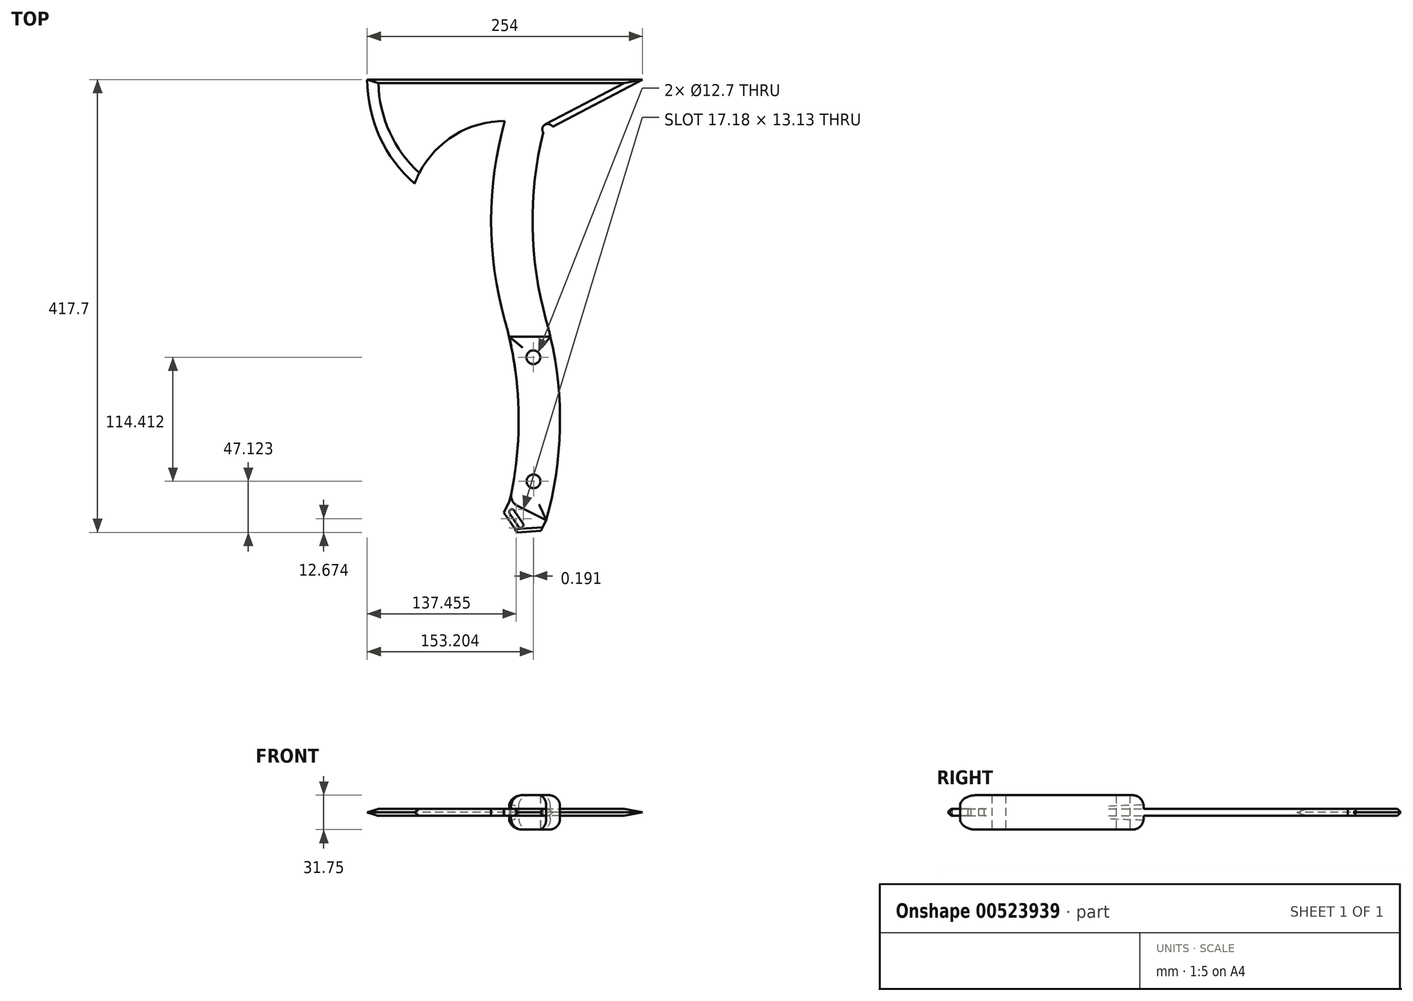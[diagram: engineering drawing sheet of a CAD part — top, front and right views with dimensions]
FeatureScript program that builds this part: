
annotation { "Feature Type Name" : "Feature", "Feature Type Description" : "" }
export const myFeature = defineFeature(function(context is Context, id is Id, definition is map)
    precondition{}
    {
        {
            var Q0;
            Q0=qCreatedBy(makeId("Top.planeOp"),FACE);
            var sketch = newSketch(context, id + "F0", { "sketchPlane" : qUnion([Q0])});
            skLineSegment(sketch, "E0.top", {"start": v(0, 496.54) * mm, "end": v(-254, 496.54) * mm});
            skLineSegment(sketch, "E1.top", {"start": v(-254, 496.54) * mm, "end": v(-139.7, 496.54) * mm});
            skLineSegment(sketch, "E2.bottom", {"start": v(-127, 496.54) * mm, "end": v(-88.9, 496.54) * mm});
            skLineSegment(sketch, "E3.bottom", {"start": v(-127, 496.54) * mm, "end": v(-139.7, 496.54) * mm});
            skArc(sketch, "E4.trimOffspring", {"start": v(-254, 496.54) * mm, "mid": v(-242.55, 443.85) * mm, "end": v(-210.28, 400.66) * mm});
            skArc(sketch, "E5", {"start": v(-127, 458.44) * mm, "mid": v(-177.68, 442.58) * mm, "end": v(-210.28, 400.66) * mm});
            skArc(sketch, "E6", {"start": v(-127, 458.44) * mm, "mid": v(-139.7, 366.37) * mm, "end": v(-127, 274.3) * mm});
            skArc(sketch, "E7", {"start": v(-91.54, 448.48) * mm, "mid": v(-101.56, 361.21) * mm, "end": v(-88.9, 274.3) * mm});
            skArc(sketch, "E8", {"start": v(-88.9, 90.14) * mm, "mid": v(-76.2, 182.22) * mm, "end": v(-88.9, 274.3) * mm});
            skArc(sketch, "E9", {"start": v(-121.56, 112.3) * mm, "mid": v(-114.5, 193.63) * mm, "end": v(-127, 274.3) * mm});
            skLineSegment(sketch, "E10", {"start": v(0, 496.54) * mm, "end": v(-91.54, 448.48) * mm});
            skPoint(sketch, "E11.end.orphan", {"position": v(-88.9, 449.87) * mm});
            skPoint(sketch, "E12.orphan", {"position": v(-88.9, 458.44) * mm});
            skLineSegment(sketch, "E13.0", {"start": v(-88.9, 90.14) * mm, "end": v(-93.76, 80.28) * mm});
            skLineSegment(sketch, "E13.1", {"start": v(-93.76, 80.28) * mm, "end": v(-115.71, 78.84) * mm});
            skLineSegment(sketch, "E13.2", {"start": v(-115.71, 78.84) * mm, "end": v(-127.94, 97.13) * mm});
            skLineSegment(sketch, "E13.3", {"start": v(-127.94, 97.13) * mm, "end": v(-123.07, 107) * mm});
            skPoint(sketch, "E13.0.midPoint", {"position": v(-88.9, 90.14) * mm});
            skLineSegment(sketch, "E14", {"start": v(-123.07, 107) * mm, "end": v(-121.56, 112.3) * mm});
            skLineSegment(sketch, "E15", {"start": v(-88.9, 90.14) * mm, "end": v(-123.07, 107) * mm});
            skPoint(sketch, "E16.orphan", {"position": v(-94.6, 92.95) * mm});
            skLineSegment(sketch, "E17.MirrorCS", {"start": v(-118.5, 99.02) * mm, "end": v(-110.36, 86.83) * mm});
            skLineSegment(sketch, "E18.MirrorCS", {"start": v(-122.73, 96.2) * mm, "end": v(-114.58, 84) * mm});
            skArc(sketch, "E19.MirrorCS", {"start": v(-110.36, 86.83) * mm, "mid": v(-111.06, 83.3) * mm, "end": v(-114.58, 84) * mm});
            skArc(sketch, "E20.MirrorCS", {"start": v(-122.73, 96.2) * mm, "mid": v(-122.03, 99.72) * mm, "end": v(-118.5, 99.02) * mm});
            skSolve(sketch);
        }
        {
            var Q0;
            Q0=makeQuery(id+"F0.imprint","IMPRINT",FACE,{"disambiguationData":[TD([[makeQuery(id+"F0.imprint","IMPRINT",EDGE,{"derivedFrom":sQuery(id+"F0.wireOp",EDGE,"E0.top")}),1.0]])]});
            var Q1;
            Q1=makeQuery(id+"F0.imprint","IMPRINT",FACE,{"disambiguationData":[TD([[makeQuery(id+"F0.imprint","IMPRINT",EDGE,{"derivedFrom":sQuery(id+"F0.wireOp",EDGE,"E13.0")}),-1.0]])]});
            extrude(context, id + "F1", {"entities" : qUnion([Q0, Q1]), "depth" : 6.35 * mm, "offsetDistance" : 25.4 * mm});
        }
        {
            var Q0;
            Q0=makeQuery(id+"F1.opExtrude","CAP_EDGE",EDGE,{"disambiguationData":[OSD([sQuery(id+"F0.wireOp",EDGE,"E4.trimOffspring")])],"isStart":false});
            var Q1;
            Q1=makeQuery(id+"F1.opExtrude","CAP_EDGE",EDGE,{"disambiguationData":[OSD([sQuery(id+"F0.wireOp",EDGE,"E4.trimOffspring")])],"isStart":true});
            chamfer(context, id + "F2", {"entities" : qUnion([Q0, Q1]), "chamferType" : ChamferType.TWO_OFFSETS, "width1" : 3.17 * mm, "oppositeDirection" : true, "width2" : 10.16 * mm, "tangentPropagation" : true});
        }
        {
            var Q0;
            Q0=makeQuery(id+"F1.opExtrude","CAP_EDGE",EDGE,{"disambiguationData":[OSD([sQuery(id+"F0.wireOp",EDGE,"E10")])],"isStart":false});
            var Q1;
            Q1=makeQuery(id+"F1.opExtrude","CAP_EDGE",EDGE,{"disambiguationData":[OSD([sQuery(id+"F0.wireOp",EDGE,"E10")])],"isStart":true});
            chamfer(context, id + "F3", {"entities" : qUnion([Q0, Q1]), "chamferType" : ChamferType.TWO_OFFSETS, "width1" : 3.17 * mm, "oppositeDirection" : false, "width2" : 5.08 * mm, "tangentPropagation" : true});
        }
        {
            var Q0;
            Q0=makeQuery(id+"F1.opExtrude","CAP_FACE",FACE,{"disambiguationData":[OSD([sQuery(id+"F0.wireOp",EDGE,"E0.top"),sQuery(id+"F0.wireOp",EDGE,"E1.top"),sQuery(id+"F0.wireOp",EDGE,"E3.bottom"),sQuery(id+"F0.wireOp",EDGE,"E4.trimOffspring"),sQuery(id+"F0.wireOp",EDGE,"E5"),sQuery(id+"F0.wireOp",EDGE,"E2.bottom"),sQuery(id+"F0.wireOp",EDGE,"E6"),sQuery(id+"F0.wireOp",EDGE,"E7"),sQuery(id+"F0.wireOp",EDGE,"E8"),sQuery(id+"F0.wireOp",EDGE,"E9"),sQuery(id+"F0.wireOp",EDGE,"E10"),sQuery(id+"F0.wireOp",EDGE,"E13.0"),sQuery(id+"F0.wireOp",EDGE,"E13.1"),sQuery(id+"F0.wireOp",EDGE,"E13.2"),sQuery(id+"F0.wireOp",EDGE,"E13.3"),sQuery(id+"F0.wireOp",EDGE,"E14"),sQuery(id+"F0.wireOp",EDGE,"E17.MirrorCS"),sQuery(id+"F0.wireOp",EDGE,"E18.MirrorCS"),sQuery(id+"F0.wireOp",EDGE,"E19.MirrorCS"),sQuery(id+"F0.wireOp",EDGE,"E20.MirrorCS")])],"isStart":false});
            var sketch = newSketch(context, id + "F4", { "sketchPlane" : qUnion([Q0])});
            skCircle(sketch, "E21", {"center": v(-87.45, 450.62) * mm, "radius": 5.08 * mm});
            skSolve(sketch);
        }
        {
            var Q0;
            Q0=sQuery(id+"F4.wireOp",VERTEX,"E21.center");
            var Q1;
            Q1=makeQuery(id+"F1.opExtrude","SWEPT_BODY",BODY,{"disambiguationData":[OSD([sQuery(id+"F0.wireOp",EDGE,"E0.top"),sQuery(id+"F0.wireOp",EDGE,"E1.top"),sQuery(id+"F0.wireOp",EDGE,"E3.bottom"),sQuery(id+"F0.wireOp",EDGE,"E4.trimOffspring"),sQuery(id+"F0.wireOp",EDGE,"E5"),sQuery(id+"F0.wireOp",EDGE,"E2.bottom"),sQuery(id+"F0.wireOp",EDGE,"E6"),sQuery(id+"F0.wireOp",EDGE,"E7"),sQuery(id+"F0.wireOp",EDGE,"E8"),sQuery(id+"F0.wireOp",EDGE,"E9"),sQuery(id+"F0.wireOp",EDGE,"E10"),sQuery(id+"F0.wireOp",EDGE,"E13.0"),sQuery(id+"F0.wireOp",EDGE,"E13.1"),sQuery(id+"F0.wireOp",EDGE,"E13.2"),sQuery(id+"F0.wireOp",EDGE,"E13.3"),sQuery(id+"F0.wireOp",EDGE,"E14"),sQuery(id+"F0.wireOp",EDGE,"E17.MirrorCS"),sQuery(id+"F0.wireOp",EDGE,"E18.MirrorCS"),sQuery(id+"F0.wireOp",EDGE,"E19.MirrorCS"),sQuery(id+"F0.wireOp",EDGE,"E20.MirrorCS")])]});
            hole(context, id + "F5", {"style" : HoleStyle.SIMPLE, "endStyle" : HoleEndStyle.THROUGH, "holeDiameter" : 10.16 * mm, "isTappedThrough" : true, "tappedDepth" : 12.7 * mm, "tapClearance" : 3, "locations" : qUnion([Q0]), "scope" : qUnion([Q1])});
        }
        {
            var Q0;
            Q0=makeQuery(id+"F1.opExtrude","CAP_FACE",FACE,{"disambiguationData":[OSD([sQuery(id+"F0.wireOp",EDGE,"E0.top"),sQuery(id+"F0.wireOp",EDGE,"E1.top"),sQuery(id+"F0.wireOp",EDGE,"E3.bottom"),sQuery(id+"F0.wireOp",EDGE,"E4.trimOffspring"),sQuery(id+"F0.wireOp",EDGE,"E5"),sQuery(id+"F0.wireOp",EDGE,"E2.bottom"),sQuery(id+"F0.wireOp",EDGE,"E6"),sQuery(id+"F0.wireOp",EDGE,"E7"),sQuery(id+"F0.wireOp",EDGE,"E8"),sQuery(id+"F0.wireOp",EDGE,"E9"),sQuery(id+"F0.wireOp",EDGE,"E10"),sQuery(id+"F0.wireOp",EDGE,"E13.0"),sQuery(id+"F0.wireOp",EDGE,"E13.1"),sQuery(id+"F0.wireOp",EDGE,"E13.2"),sQuery(id+"F0.wireOp",EDGE,"E13.3"),sQuery(id+"F0.wireOp",EDGE,"E14"),sQuery(id+"F0.wireOp",EDGE,"E17.MirrorCS"),sQuery(id+"F0.wireOp",EDGE,"E18.MirrorCS"),sQuery(id+"F0.wireOp",EDGE,"E19.MirrorCS"),sQuery(id+"F0.wireOp",EDGE,"E20.MirrorCS")])],"isStart":false});
            var sketch = newSketch(context, id + "F6", { "sketchPlane" : qUnion([Q0])});
            skLineSegment(sketch, "E22", {"start": v(-88.9, 90.14) * mm, "end": v(-123.07, 107) * mm});
            skLineSegment(sketch, "E23", {"start": v(-123.07, 259.4) * mm, "end": v(-85.07, 259.4) * mm});
            skArc(sketch, "E24", {"start": v(-123.07, 107) * mm, "mid": v(-114.43, 183.2) * mm, "end": v(-123.07, 259.4) * mm});
            skArc(sketch, "E25", {"start": v(-88.9, 90.14) * mm, "mid": v(-75.96, 174.52) * mm, "end": v(-85.07, 259.4) * mm});
            skCircle(sketch, "E26", {"center": v(-100.6, 125.96) * mm, "radius": 6.35 * mm});
            skCircle(sketch, "E27", {"center": v(-100.8, 240.37) * mm, "radius": 6.35 * mm});
            skSolve(sketch);
        }
        {
            var Q0;
            {var subQ5=sQuery(id+"F6.wireOp",EDGE,"E22");Q0=makeQuery(id+"F6.imprint","IMPRINT",FACE,{"disambiguationData":[TD([[makeQuery(id+"F6.imprint","IMPRINT",EDGE,{"derivedFrom":subQ5}),-1.0]])]});}
            extrude(context, id + "F7", {"entities" : qUnion([Q0]), "operationType" : NewBodyOperationType.ADD, "depth" : 12.7 * mm, "offsetDistance" : 25.4 * mm});
        }
        {
            var Q0;
            Q0=makeQuery(id+"F7.opExtrude","CAP_FACE",FACE,{"disambiguationData":[OSD([sQuery(id+"F0.wireOp",EDGE,"E8"),sQuery(id+"F0.wireOp",EDGE,"E9"),sQuery(id+"F0.wireOp",EDGE,"E14"),sQuery(id+"F6.wireOp",EDGE,"E22"),sQuery(id+"F6.wireOp",EDGE,"E23"),sQuery(id+"F6.wireOp",EDGE,"E24"),sQuery(id+"F6.wireOp",EDGE,"E26"),sQuery(id+"F6.wireOp",EDGE,"E27")])],"isStart":false});
            var sketch = newSketch(context, id + "F8", { "sketchPlane" : qUnion([Q0])});
            skCircle(sketch, "E28", {"center": v(-100.6, 125.96) * mm, "radius": 6.35 * mm});
            skPoint(sketch, "E28.first.point", {"position": v(-106.92, 126.6) * mm});
            skPoint(sketch, "E28.second.point", {"position": v(-94.3, 125.22) * mm});
            skPoint(sketch, "E28.third.point", {"position": v(-100.97, 119.62) * mm});
            skCircle(sketch, "E29", {"center": v(-100.8, 240.37) * mm, "radius": 6.35 * mm});
            skPoint(sketch, "E29.first.point", {"position": v(-100.97, 234.03) * mm});
            skPoint(sketch, "E29.second.point", {"position": v(-100.4, 246.71) * mm});
            skPoint(sketch, "E29.third.point", {"position": v(-106.96, 241.9) * mm});
            skSolve(sketch);
        }
        {
            var Q0;
            Q0=sQuery(id+"F8.wireOp",VERTEX,"E29.center");
            var Q1;
            Q1=sQuery(id+"F8.wireOp",VERTEX,"E28.center");
            var Q2;
            Q2=makeQuery(id+"F1.opExtrude","SWEPT_BODY",BODY,{"disambiguationData":[OSD([sQuery(id+"F0.wireOp",EDGE,"E0.top"),sQuery(id+"F0.wireOp",EDGE,"E1.top"),sQuery(id+"F0.wireOp",EDGE,"E3.bottom"),sQuery(id+"F0.wireOp",EDGE,"E4.trimOffspring"),sQuery(id+"F0.wireOp",EDGE,"E5"),sQuery(id+"F0.wireOp",EDGE,"E2.bottom"),sQuery(id+"F0.wireOp",EDGE,"E6"),sQuery(id+"F0.wireOp",EDGE,"E7"),sQuery(id+"F0.wireOp",EDGE,"E8"),sQuery(id+"F0.wireOp",EDGE,"E9"),sQuery(id+"F0.wireOp",EDGE,"E10"),sQuery(id+"F0.wireOp",EDGE,"E13.0"),sQuery(id+"F0.wireOp",EDGE,"E13.1"),sQuery(id+"F0.wireOp",EDGE,"E13.2"),sQuery(id+"F0.wireOp",EDGE,"E13.3"),sQuery(id+"F0.wireOp",EDGE,"E14"),sQuery(id+"F0.wireOp",EDGE,"E17.MirrorCS"),sQuery(id+"F0.wireOp",EDGE,"E18.MirrorCS"),sQuery(id+"F0.wireOp",EDGE,"E19.MirrorCS"),sQuery(id+"F0.wireOp",EDGE,"E20.MirrorCS")])]});
            hole(context, id + "F9", {"style" : HoleStyle.SIMPLE, "endStyle" : HoleEndStyle.THROUGH, "holeDiameter" : 12.7 * mm, "isTappedThrough" : true, "tappedDepth" : 12.7 * mm, "tapClearance" : 3, "locations" : qUnion([Q0, Q1]), "scope" : qUnion([Q2])});
        }
        {
            var Q0;
            Q0=makeQuery(id+"F7.opExtrude","CAP_FACE",FACE,{"disambiguationData":[OSD([sQuery(id+"F0.wireOp",EDGE,"E8"),sQuery(id+"F0.wireOp",EDGE,"E9"),sQuery(id+"F0.wireOp",EDGE,"E14"),sQuery(id+"F6.wireOp",EDGE,"E22"),sQuery(id+"F6.wireOp",EDGE,"E23"),sQuery(id+"F6.wireOp",EDGE,"E24"),sQuery(id+"F6.wireOp",EDGE,"E26"),sQuery(id+"F6.wireOp",EDGE,"E27")])],"isStart":false});
            extrude(context, id + "F10", {"entities" : qUnion([Q0]), "operationType" : NewBodyOperationType.ADD, "oppositeDirection" : true, "depth" : 31.75 * mm, "offsetDistance" : 25.4 * mm});
        }
        {
            var Q0;
            Q0=makeQuery(id+"F7.opExtrude","CAP_EDGE",EDGE,{"disambiguationData":[OSD([sQuery(id+"F6.wireOp",EDGE,"E22")])],"isStart":false});
            var Q1;
            Q1=makeQuery(id+"F7.opExtrude","CAP_EDGE",EDGE,{"disambiguationData":[OSD([sQuery(id+"F0.wireOp",EDGE,"E8")])],"isStart":false});
            var Q2;
            Q2=makeQuery(id+"F7.opExtrude","CAP_EDGE",EDGE,{"disambiguationData":[OSD([sQuery(id+"F6.wireOp",EDGE,"E23")])],"isStart":false});
            fillet(context, id + "F11", {"entities" : qUnion([Q0, Q1, Q2]), "radius" : 10.16 * mm, "tangentPropagation" : true, "allowEdgeOverflow" : false});
        }
        {
            var Q0;
            Q0=makeQuery(id+"F7.opExtrude","CAP_EDGE",EDGE,{"disambiguationData":[OSD([sQuery(id+"F0.wireOp",EDGE,"E9")])],"isStart":false});
            fillet(context, id + "F12", {"entities" : qUnion([Q0]), "radius" : 10.16 * mm, "tangentPropagation" : true, "allowEdgeOverflow" : false});
        }
        {
            var Q0;
            Q0=makeQuery(id+"F10.opExtrude","CAP_EDGE",EDGE,{"disambiguationData":[OSD([sQuery(id+"F0.wireOp",EDGE,"E8")])],"isStart":false});
            var Q1;
            Q1=makeQuery(id+"F10.opExtrude","CAP_EDGE",EDGE,{"disambiguationData":[OSD([sQuery(id+"F6.wireOp",EDGE,"E22")])],"isStart":false});
            var Q2;
            Q2=makeQuery(id+"F10.opExtrude","CAP_EDGE",EDGE,{"disambiguationData":[OSD([sQuery(id+"F6.wireOp",EDGE,"E23")])],"isStart":false});
            fillet(context, id + "F13", {"entities" : qUnion([Q0, Q1, Q2]), "radius" : 10.16 * mm, "tangentPropagation" : true, "allowEdgeOverflow" : false});
        }
        {
            var Q0;
            Q0=makeQuery(id+"F10.opExtrude","CAP_EDGE",EDGE,{"disambiguationData":[OSD([sQuery(id+"F0.wireOp",EDGE,"E9")])],"isStart":false});
            fillet(context, id + "F14", {"entities" : qUnion([Q0]), "radius" : 10.16 * mm, "tangentPropagation" : true, "allowEdgeOverflow" : false});
        }
        {
            var Q0;
            Q0=makeQuery(id+"F1.opExtrude","CAP_EDGE",EDGE,{"disambiguationData":[OSD([sQuery(id+"F0.wireOp",EDGE,"E13.1")])],"isStart":false});
            var Q1;
            Q1=makeQuery(id+"F1.opExtrude","CAP_EDGE",EDGE,{"disambiguationData":[OSD([sQuery(id+"F0.wireOp",EDGE,"E13.1")])],"isStart":true});
            chamfer(context, id + "F15", {"entities" : qUnion([Q0, Q1]), "width" : 3.17 * mm, "tangentPropagation" : true});
        }
        {
            var Q0;
            Q0=makeQuery(id+"F1.opExtrude","CAP_EDGE",EDGE,{"disambiguationData":[OSD([sQuery(id+"F0.wireOp",EDGE,"E0.top"),sQuery(id+"F0.wireOp",EDGE,"E1.top"),sQuery(id+"F0.wireOp",EDGE,"E3.bottom"),sQuery(id+"F0.wireOp",EDGE,"E2.bottom")])],"isStart":false});
            var Q1;
            Q1=makeQuery(id+"F1.opExtrude","CAP_EDGE",EDGE,{"disambiguationData":[OSD([sQuery(id+"F0.wireOp",EDGE,"E0.top"),sQuery(id+"F0.wireOp",EDGE,"E1.top"),sQuery(id+"F0.wireOp",EDGE,"E3.bottom"),sQuery(id+"F0.wireOp",EDGE,"E2.bottom")])],"isStart":true});
            chamfer(context, id + "F16", {"entities" : qUnion([Q0, Q1]), "width" : 3.17 * mm, "tangentPropagation" : true});
        }
    });
